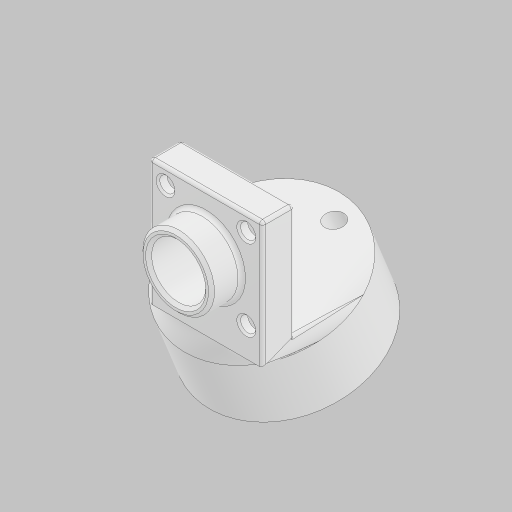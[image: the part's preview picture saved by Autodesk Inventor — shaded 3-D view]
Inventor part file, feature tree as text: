
AUTODESK INVENTOR PART (.ipt)
format: ipt  version: 2023.5 (Build 275446000, 446)  size: 635,392 bytes
history: native  units: in
note: dims shown in document units (in); Inventor stores cm internally (conversion verified against a paired STEP export)
features: extrude x12, sketch x10, projected_geometry x10, fillet x6, plane x3, hole x3, chamfer x3, other x3, thicken_offset x2, loft x1, sweep x1, revolve x1
ambient origin geometry x8: Origin, YZ Plane, XZ Plane, XY Plane, X Axis, Y Axis, Z Axis, Center Point
bodies: Solid1 (feature_tree)
feature tree (55):
  extrude  "Extrusion1"  Depth=0.525in
  extrude  "Extrusion2"  Depth=0.4673in
  plane  "Work Plane1"
  extrude  "Extrusion3"  Depth=0.6in
  loft  "Loft1"
  extrude  "Extrusion4"  TaperAngle=0.0deg  [1 undecoded]
  hole  "Hole1"  [1 undecoded]
  extrude  "Extrusion5"  Depth=1.0in
  extrude  "Extrusion6"  Depth=1.0in
  hole  "Hole2"  [1 undecoded]
  plane  "Work Plane2"
  fillet  "Fillet1"  Radius=0.15in
  chamfer  "Chamfer1"  Distance=0.9792in
  fillet  "Fillet2"  Radius=0.9792in
  extrude  "Extrusion7"  TaperAngle=300.0deg  [1 undecoded]
  fillet  "Fillet3"  Radius=0.05in
  chamfer  "Chamfer2"  Distance=0.05in Angle=45.0deg
  thicken_offset  "Thicken1"
  hole  "Hole4"  [1 undecoded]
  extrude  "Extrusion12"  Depth=1.0in
  chamfer  "Chamfer3"  Distance=1.0in
  extrude  "Extrusion8"  Depth=1.0in
  sketch  "Sketch13"  dims[d5=1.875in d6=0.0in d7=0.6in]
  sketch  "3D Sketch1"
  extrude  "Extrusion9"  Depth=1.0in TaperAngle=45.0deg
  extrude  "Extrusion10"  Depth=1.0in
  sketch  "Sketch15"  dims[d12=0.0in d13=90.0deg d14=0.0in d15=90.0deg]
  plane  "Work Plane3"
  sketch  "Sketch16"  dims[d16=1.6in d17=0.3in d18=0.0in]
  sweep  "Sweep1"
  fillet  "Fillet6"  Radius=1.0in
  thicken_offset  "Thicken2"
  fillet  "Fillet7"  Radius=1.0in
  extrude  "Extrusion11"  Depth=1.0in
  fillet  "Fillet9"  Radius=0.87in
  other  "Edges1"
  other  "Edges2"
  projected_geometry  "Projected Loop1"
  projected_geometry  "Projected Loop2"
  sketch  "Sketch11"  dims[d0=1.875in d1=0.525in]
  other  "Srf1"
  sketch  "Sketch12"  dims[d2=1.875in d3=0.0in d4=0.4673in]
  projected_geometry  "Projected Loop3"
  sketch  "Sketch14"  dims[d9=2.75in d10=0.1in d11=0.0in]
  projected_geometry  "Projected Loop4"
  sketch  "3D Sketch2"
  sketch  "Sketch17"  dims[d19=0.9in d20=0.75in d21=0.119in d22=0.25in d23=0.6871in d24=1.0in d25=0.8108in d26=1.1875in]
  sketch  "Sketch18"  dims[d27=0.5in d28=0.0in d29=0.1839in d30=1.3386in d31=0.15in d32=0.0in d33=0.094in d34=0.75in d35=0.251in d36=0.15in d37=0.6871in d38=1.0in d39=0.8108in d40=0.9792in d41=0.9792in d42=300.0deg d52=0.05in d53=0.05in d54=0.125in d55=45.0deg d56=0.0625in d57=1.0in d58=1.0in d59=0.0in d60=0.25in d61=0.0312in d62=0.125in d63=45.0deg d64=0.2405in d65=90.0deg d66=1.0in d67=1.0in d68=0.177in d69=0.75in d70=0.313in d71=1.45in d72=0.5635in d73=1.0in d74=0.8108in d75=1.25in d76=0.87in d77=1.0in d78=0.0in d79=0.1875in d80=1.5in d81=0.0in d82=0.1875in d83=0.25in d84=0.0in d85=0.1875in d86=0.1875in d87=0.0in d88=0.0in d92=0.0312in d93=0.1in d94=0.1in d95=0.0156in d97=0.1875in d98=0.1875in d99=0.1875in d100=0.1875in d101=0.0in d102=0.0312in d103=1.125in d104=1.0in d105=0.0in d106=0.25in d107=0.125in d108=45.0deg]
  revolve  "RevolutionSrf1"  [1 undecoded]
  projected_geometry  "Project Cut Edges1"
  projected_geometry  "Project Cut Edges2"
  projected_geometry  "Project Cut Edges3"
  projected_geometry  "Project Cut Edges4"
  projected_geometry  "Project Cut Edges5"
  projected_geometry  "Project Cut Edges6"
note: 6 required parameter values undecoded (feature->parameter linkage not recoverable at this tier; creation-order binding heuristic only, values carry confidence <= 0.55)